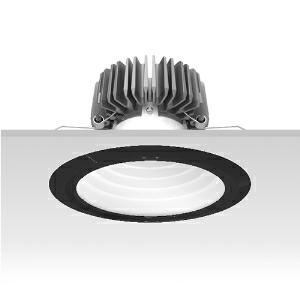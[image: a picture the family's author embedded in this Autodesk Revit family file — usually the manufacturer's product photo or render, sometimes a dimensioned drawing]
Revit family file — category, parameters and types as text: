
# Revit family: 3f_filippi_-_3f_reno_bianco_ampio_3f_filippi_-_30629_a01026_-_3f_reno_200_wh_3000-840_wide___vt_bk_5dbe
name_source: partatom
category: Lighting Fixtures
units: mm (PartAtom-declared; Revit-internal decimal feet)

## family parameters
Cut with Voids When Loaded = No
Host = Face
Light Source = No
Part Type = Normal
Room Calculation Point = No
Round Connector Dimension = Use Diameter
Shared = No

## types (1)
- 3F Filippi - 3F Reno Bianco Ampio (1 x LED, 2529 lm, 28 W, 4000 K)
    Apparent Load = 28 VA
    Approval mark = CE
    CIE Flux Codes = 75 94 99 100 100
    Color Rendering = 80
    Color Temperature = 4000 K
    Control Gear = Electronic ballast
    Default Elevation = 1800 mm
    Description = ILLUMINOTECHNICAL
Luminous efficiency 100% (DLOR 100%, ULOR 0%).
Initial luminous flux of the luminaire 2529 lm.
Direct symmetric wide distribution.
Installation Interdistance Transv.D = 1.56 x hu - Long.D = 1.56 x hu.
Tabular UGR (CIE 117 - 4H-8H; S=0.25H; 70/50/20): RUG 21.8 - 21.7.
Beam angle: 74° - 74°.
Luminous efficacy 90 lm/W.
Lifetime (L90/B10): 30000 h. (tq+25°C)
Lifetime (L85/B10): 50000 h. (tq+25°C)
Lifetime (L70/B10): 80000 h. (tq+25°C)
Sudden decreased luminous flux after 50000 hours: 0% (C0).
Photobiological safety in compliance with IEC/TR 62778: RG0 risk exempt, (IEC 62471).
In compliance with IEC/EN 62722-2-1 - IEC/EN 62717 standards.

SOURCE
Compact LED module 3000/840.
Energy efficiency class (UE 2019/2020 - UE 2019/2015): D.
CIE 13.3 Colour rendering index: CRI >80 (R9 <50%).
IES TM-30 Fidelity Index: Rf = 84 Rg = 95.
CCT nominal colour temperature 4000 K.
Colour initial tolerance (MacAdam): SDCM 3.
Zhaga Book 3 compliant.

MECHANICAL
Passive heat dissipator in die-casting aluminium, oversized, for optimum thermal management of the LED module.
Parabolic element with graduated/concentric rings in white polycarbonate.
Transparent external lens with glossy and satin differentiated surfaces, with a cooling and anti-insect system in methacrylate (PMMA).
Fastening spring clips in stainless steel.
Dimensions: diameter 226 mm, height 146 mm. Weight 1.69 kg.
IP44 protection degree for exposed part, IP20 for recessed part.
Mechanical strength to impacts IK06 (1 joule).
Glow-wire test resistance 650°C.

ELECTRICAL
Wiring on a separate unit.
Halogen Free electronic wiring 230V-50/60Hz, power factor 0.95, THD <25%, constant output current, SELV, class II, 1 driver.
Power of the luminaire 28 W.
ENEC - CE.
SAFE FLICKER: PstLM=<1 and SVM=<0.4 (IEC TR 61547-1 and IEC TR 63158), to ensure a more comfortable and safe light.
Luminaire compliant with EN 60598-2-22 for power supply from a centralised emergency system CPSS (Central Power Supply System), not incorporated in the luminaire - high risk areas excluded. The default power and flux are 100% in AC and 100% in DC.
Ambient temperature from 0°C to +25°C.
Temperature class T6 max 85°C.
Relative humidity UR: <85%.

INSTALLATION
Pull-up recessed fitting.
False ceiling carving: 200 mm.
All accessories dedicated to this product are available on the Catalog and on our website www.3F-Filippi.com.

ACCESSORIES
A01026 - VT transparent glass, tempered, not flammable, locked and in line with the trim, in black polycarbonate.

APPLICATIONS
Environments: architectural, commercial, exhibition areas, transit areas, corridors, shops, display windows, service areas.
In false ceilings with narrow voids.

WARNING
Luminaire designed for disposal/recycling at end-of-life.
Replaceable (LED only) light source by a professional. Replaceable control gear by a professional.
    Height = 0 mm  [stored 0 ft]
    Lamp = 1 x LED
    Lamp Light Flux = 2529 lm
    Lamp Power = 28 W
    Lamp count = 1
    Length = 226 mm
    Lifetime = 50000 h
    Luminous efficacy = 90 lm/W
    Manufacturer = 3F Filippi
    ModVariant = No
    Model = 3F Filippi - 30629+A01026 - 3F Reno 200 WH 3000-840 WIDE + VT BK
    Mounting Place = Ceiling
    Mounting Type = Recessed
    Number of Poles = 1
    OnlyDefault = Yes
    Power Factor = 1
    Product Name = 3F Filippi - 3F Reno Bianco Ampio
    Product group = recessed luminaire
    ProductGroupID = 4
    Protection Class = Protection class II
    Protection Degree = IP 20
    RLX_Detail_Level = 1
    RLX_Emergency_Light_Flux = 0 lm
    RLX_Emergency_Type = 0
    RLX_Emergency_Type_DB = No
    RlxData = <blob elided: 101221 chars, md5=87691b95>
    Socket = socket
    Standby Power = 0 W
    System Light Flux = 2529 lm
    System Power = 28 W
    Type Comments = Product without accessories
    Type Image = 3ffilippi_3f_reno_200_wh__a01026.jpg
    URL = http://relux.com
    VarID = ---
    Voltage = 0 V
    Weight = 0.00 kg
    Width = 0 mm  [stored 0 ft]

note: [stored X ft] marks values corroborated as IEEE doubles in the binary element streams (Revit-internal decimal feet)

## geometry (parser evidence)
native form markers: Blend x4, Sweep x10
no freeform markers — native parametric forms only
